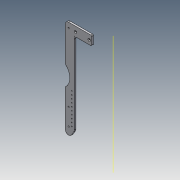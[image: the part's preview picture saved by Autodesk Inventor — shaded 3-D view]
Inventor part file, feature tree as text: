
AUTODESK INVENTOR PART (.ipt)
format: ipt  version: 2018.3 (Build 223284000, 284)  size: 220,672 bytes
history: native  units: in
note: dims shown in document units (in); Inventor stores cm internally (conversion verified against a paired STEP export)
features: other x9, extrude x4, hole x4, fillet x4, chamfer x3, mirror x1, sketch x1, pattern_linear x1, plane x1
ambient origin geometry x8: Origin, YZ Plane, XZ Plane, XY Plane, X Axis, Y Axis, Z Axis, Center Point
bodies: Solid1 (feature_tree)
feature tree (28):
  extrude  "Extrusion1"  Depth=0.25in TaperAngle=0.0deg
  hole  "Hole5"  [1 undecoded]
  extrude  "Extrusion5"  Depth=0.125in
  chamfer  "Chamfer3"  Distance=7.0in
  chamfer  "Chamfer4"  Distance=11.3in
  fillet  "Fillet8"  Radius=13.0in
  fillet  "Fillet6"  Radius=11.375in
  fillet  "Fillet7"  [1 undecoded]
  extrude  "Extrusion6"  Depth=0.125in TaperAngle=0.0deg
  hole  "Hole6"  [1 undecoded]
  mirror  "Mirror1"
  hole  "Hole7"  [1 undecoded]
  sketch  "Sketch3"  dims[d2=14.0in d4=0.25in d5=0.0in d66=7.0in d70=14.5in d71=7.0in d85=11.3in d86=13.0in d87=0.201in d88=0.394in d89=0.385in d90=0.25in d91=0.5635in d92=0.559in d93=0.8108in d94=11.375in d95=0.0in d96=1.0in d97=0.0in d98=0.5in d99=0.4in d100=0.625in d101=0.125in d102=60.0deg d103=0.625in d104=0.125in d105=60.0deg d106=0.5in d107=8.25in d108=3.825in d109=1.0in d110=0.0in d111=8.25in d112=0.374in d113=0.374in d115=0.622in d116=2.825in d117=0.06in d118=0.75in d119=0.375in d120=0.25in d121=0.5635in d122=1.0in d123=0.8108in d124=5.5in d125=5.5in d126=0.177in d127=0.75in d128=0.37in d129=0.25in d130=90.0deg d131=1.0in d132=0.8108in d133=12.5in d134=6.5in d135=6.25in d136=2.0in d137=2.0in d138=12.0in d139=16.0in d140=3.125in d141=0.0in d142=0.0in d143=0.125in d144=0.95in d145=6.0in d146=0.129in d147=0.75in d148=0.225in d149=0.25in d150=0.5635in d151=1.0in d152=0.8108in d153=3.937in d155=0.5in d157=0.3625in d158=2.5in d159=2.5in d160=2.203in d161=0.096in d162=0.125in d163=45.0deg]
  extrude  "Extrusion7"  Depth=0.125in TaperAngle=60.0deg
  fillet  "Fillet9"  Radius=0.125in
  hole  "Hole8"  [1 undecoded]
  pattern_linear  "Rectangular Pattern3"  Spacing1=8.25in  [1 undecoded]
  chamfer  "Chamfer5"  Distance=3.825in
  plane  "Work Plane1"
  other  "Work Axis1"
  other  "Work Axis2"
  other  "Work Axis3"
  other  "Work Axis4"
  other  "Work Axis5"
  other  "Work Axis6"
  other  "Work Axis7"
  other  "Work Axis8"
  other  "Work Axis9"
note: 6 required parameter values undecoded (feature->parameter linkage not recoverable at this tier; creation-order binding heuristic only, values carry confidence <= 0.55)
